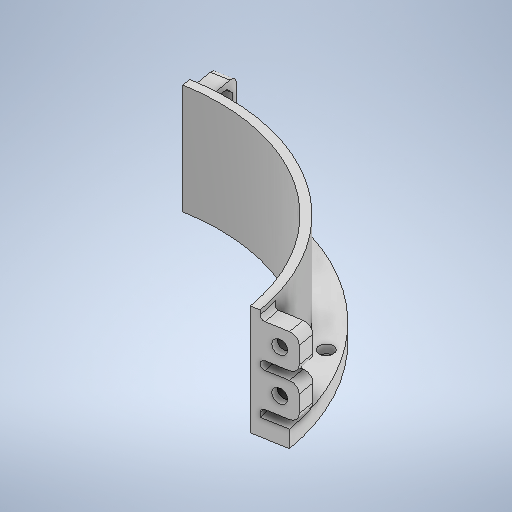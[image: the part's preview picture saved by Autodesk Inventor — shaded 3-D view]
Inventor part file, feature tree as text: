
AUTODESK INVENTOR PART (.ipt)
format: ipt  version: 2025 (Build 290162000, 162)  size: 553,472 bytes
history: native  units: in
note: dims shown in document units (in); Inventor stores cm internally (conversion verified against a paired STEP export)
features: sketch x14, extrude x11, other x3, fillet x3, hole x2
ambient origin geometry x8: Origin, YZ Plane, XZ Plane, XY Plane, X Axis, Y Axis, Z Axis, Center Point
bodies: Body1 (feature_tree)
feature tree (33):
  other  "Cylinder.ipt"
  extrude  "Extrusion1"  Depth=0.3937in
  extrude  "Extrusion2"  Depth=0.3937in TaperAngle=0.0deg
  sketch  "Sketch3"  dims[d15=0.1969in d16=0.0in d17=10.6299in]
  extrude  "Extrusion3"  Depth=10.6299in
  extrude  "Extrusion5"  Depth=0.1969in TaperAngle=0.0deg
  sketch  "Sketch6"  dims[d20=3.937in d22=360.0deg d24=0.1969in d25=0.0in]
  extrude  "Extrusion6"  Depth=10.6299in
  extrude  "Extrusion7"  Depth=0.3346in
  extrude  "Extrusion8"  Depth=0.1969in TaperAngle=0.0deg
  extrude  "Extrusion9"  TaperAngle=0.0deg  [1 undecoded]
  extrude  "Nut Bracket"  Depth=0.1969in
  fillet  "Fillet1"  Radius=10.6299in
  fillet  "Fillet2"  Radius=0.1969in
  extrude  "Nut Inserts"  TaperAngle=0.0deg  [1 undecoded]
  extrude  "Bolt Bracket"  Depth=0.1969in
  fillet  "Fillet3"  Radius=0.1969in
  hole  "Bolt Hole Bore"  [1 undecoded]
  hole  "Hole2"  [1 undecoded]
  other  "Solid12::Cylinder.ipt"
  other  "TaggingFeature1"
  sketch  "Sketch1"  dims[d0=0.3937in d2=10.2362in]
  sketch  "Sketch2"  dims[d7=11.2205in d8=10.6299in]
  sketch  "Sketch5"  dims[d18=0.2953in d19=0.3346in]
  sketch  "Sketch Circular Pattern1"  dims[d3=0.0in d4=0.0in d5=0.3937in d6=0.0in]
  sketch  "Sketch Circular Pattern2"  dims[d9=10.6299in d10=0.1969in d11=0.0in]
  sketch  "Sketch7"  dims[d27=3.937in d29=360.0deg d31=0.0in d32=0.0in]
  sketch  "Sketch8"  dims[d33=2.1654in d34=0.0in d35=10.0394in d36=10.6299in d37=0.1969in]
  sketch  "Sketch9"  dims[d38=0.0687in d39=0.0in d40=0.0in]
  sketch  "Sketch10"  dims[d43=0.8858in d44=0.7874in d45=0.1969in]
  sketch  "Sketch12"  dims[d46=0.7874in d47=0.1969in]
  sketch  "Sketch15"  dims[d48=0.1969in d49=0.1969in]
  sketch  "Sketch16"  dims[d50=0.1969in d51=0.1969in d52=0.8858in d53=0.3937in d54=0.0in d55=0.0984in d56=0.0984in d57=0.3937in d58=0.3937in d59=0.5197in d60=0.3937in d61=0.5197in d62=0.2362in d63=0.0in d71=0.8858in d72=0.8858in d73=0.7874in d74=0.7874in d75=0.1969in d76=0.1969in d77=0.7874in d78=0.1969in d79=0.3937in d80=0.0in d81=0.0984in d94=0.3937in d95=0.3937in d96=0.3937in d97=0.3937in d98=0.3228in d99=0.2362in d100=0.5197in d101=0.2362in d102=90.0deg d103=0.315in d104=0.8108in d105=0.3937in d106=0.3937in d107=0.3937in d108=0.3228in d109=0.2362in d110=0.1575in d111=0.0787in d112=90.0deg d113=0.315in d114=0.8108in]
note: 4 required parameter values undecoded (feature->parameter linkage not recoverable at this tier; creation-order binding heuristic only, values carry confidence <= 0.55)
